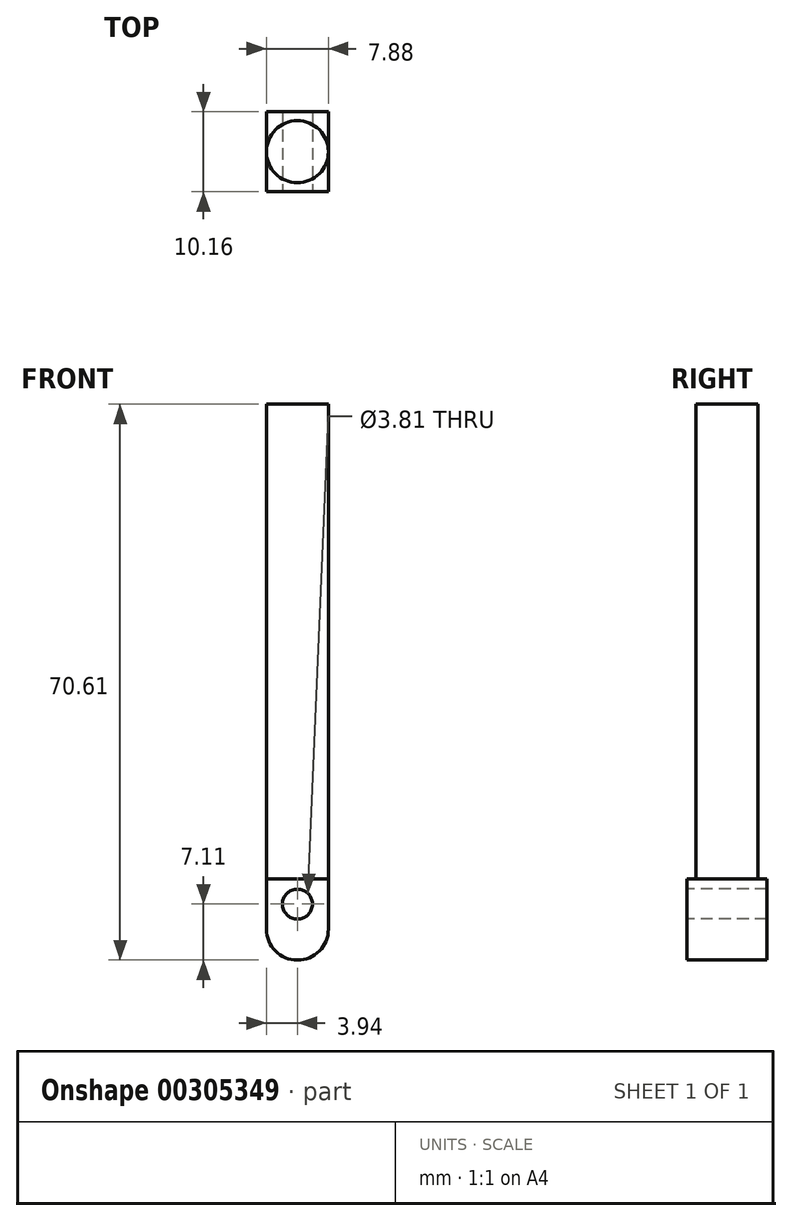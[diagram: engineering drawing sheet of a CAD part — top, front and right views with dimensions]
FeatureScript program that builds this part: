
annotation { "Feature Type Name" : "Feature", "Feature Type Description" : "" }
export const myFeature = defineFeature(function(context is Context, id is Id, definition is map)
    precondition{}
    {
        {
            var Q0;
            Q0=qCreatedBy(makeId("Front.planeOp"),FACE);
            var sketch = newSketch(context, id + "F0", { "sketchPlane" : qUnion([Q0])});
            skLineSegment(sketch, "E0.bottom", {"start": v(-3.94, 3.18) * mm, "end": v(3.94, 3.18) * mm});
            skLineSegment(sketch, "E0.top", {"start": v(-3.94, -3.18) * mm, "end": v(3.94, -3.18) * mm});
            skLineSegment(sketch, "E0.left", {"start": v(-3.94, 3.18) * mm, "end": v(-3.94, -3.17) * mm});
            skLineSegment(sketch, "E0.right", {"start": v(3.94, 3.18) * mm, "end": v(3.94, -3.17) * mm});
            skPoint(sketch, "E0.middle", {"position": v(0, 0) * mm});
            skArc(sketch, "E1", {"start": v(-3.94, -3.18) * mm, "mid": v(0, -7.11) * mm, "end": v(3.94, -3.17) * mm});
            skSolve(sketch);
        }
        {
            var Q0;
            Q0=makeQuery(id+"F0.imprint","IMPRINT",FACE,{"disambiguationData":[TD([[makeQuery(id+"F0.imprint","IMPRINT",EDGE,{"derivedFrom":sQuery(id+"F0.wireOp",EDGE,"E0.bottom")}),-1.0]])]});
            var Q1;
            Q1=makeQuery(id+"F0.imprint","IMPRINT",FACE,{"disambiguationData":[TD([[makeQuery(id+"F0.imprint","IMPRINT",EDGE,{"derivedFrom":sQuery(id+"F0.wireOp",EDGE,"E0.top")}),-1.0]])]});
            extrude(context, id + "F1", {"entities" : qUnion([Q0, Q1]), "depth" : 10.16 * mm});
        }
        {
            var Q0;
            Q0=makeQuery(id+"F1.opExtrude","CAP_FACE",FACE,{"disambiguationData":[OSD([sQuery(id+"F0.wireOp",EDGE,"E0.bottom"),sQuery(id+"F0.wireOp",EDGE,"E0.left"),sQuery(id+"F0.wireOp",EDGE,"E0.right"),sQuery(id+"F0.wireOp",EDGE,"E1")])],"isStart":false});
            var sketch = newSketch(context, id + "F2", { "sketchPlane" : qUnion([Q0])});
            skCircle(sketch, "E2", {"center": v(0, 0) * mm, "radius": 1.9 * mm});
            skSolve(sketch);
        }
        {
            var Q0;
            Q0=makeQuery(id+"F2.imprint","IMPRINT",FACE,{"disambiguationData":[TD([[makeQuery(id+"F2.imprint","IMPRINT",EDGE,{"derivedFrom":sQuery(id+"F2.wireOp",EDGE,"E2")}),1.0]])]});
            extrude(context, id + "F3", {"entities" : qUnion([Q0]), "operationType" : NewBodyOperationType.REMOVE, "endBound" : BoundingType.THROUGH_ALL, "oppositeDirection" : true, "depth" : 25.4 * mm});
        }
        {
            var Q0;
            Q0=makeQuery(id+"F1.opExtrude","SWEPT_FACE",FACE,{"disambiguationData":[OSD([sQuery(id+"F0.wireOp",EDGE,"E0.bottom")])]});
            var sketch = newSketch(context, id + "F4", { "sketchPlane" : qUnion([Q0])});
            skCircle(sketch, "E3", {"center": v(0, -5.08) * mm, "radius": 3.94 * mm});
            skPoint(sketch, "E3.centerSnap0", {"position": v(-3.94, -5.08) * mm});
            skSolve(sketch);
        }
        {
            var Q0;
            {var subQ0=sQuery(id+"F4.wireOp",EDGE,"E3");var subQ1=sQuery(id+"F0.wireOp",EDGE,"E0.bottom");var subQ2=makeQuery(id+"F4.imprint","INTERSECT",VERTEX,{"derivedFrom":[makeQuery(id+"F1.opExtrude","SWEPT_EDGE",EDGE,{"disambiguationData":[OSD([subQ1,sQuery(id+"F0.wireOp",EDGE,"E0.left")])]}),subQ0]});Q0=makeQuery(id+"F4.imprint","IMPRINT",FACE,{"disambiguationData":[TD([[makeQuery(id+"F4.imprint","IMPRINT",EDGE,{"disambiguationData":[TD([[subQ2,1.0]])],"derivedFrom":subQ0}),1.0]])]});}
            extrude(context, id + "F5", {"entities" : qUnion([Q0]), "operationType" : NewBodyOperationType.ADD, "depth" : 60.32 * mm});
        }
    });
